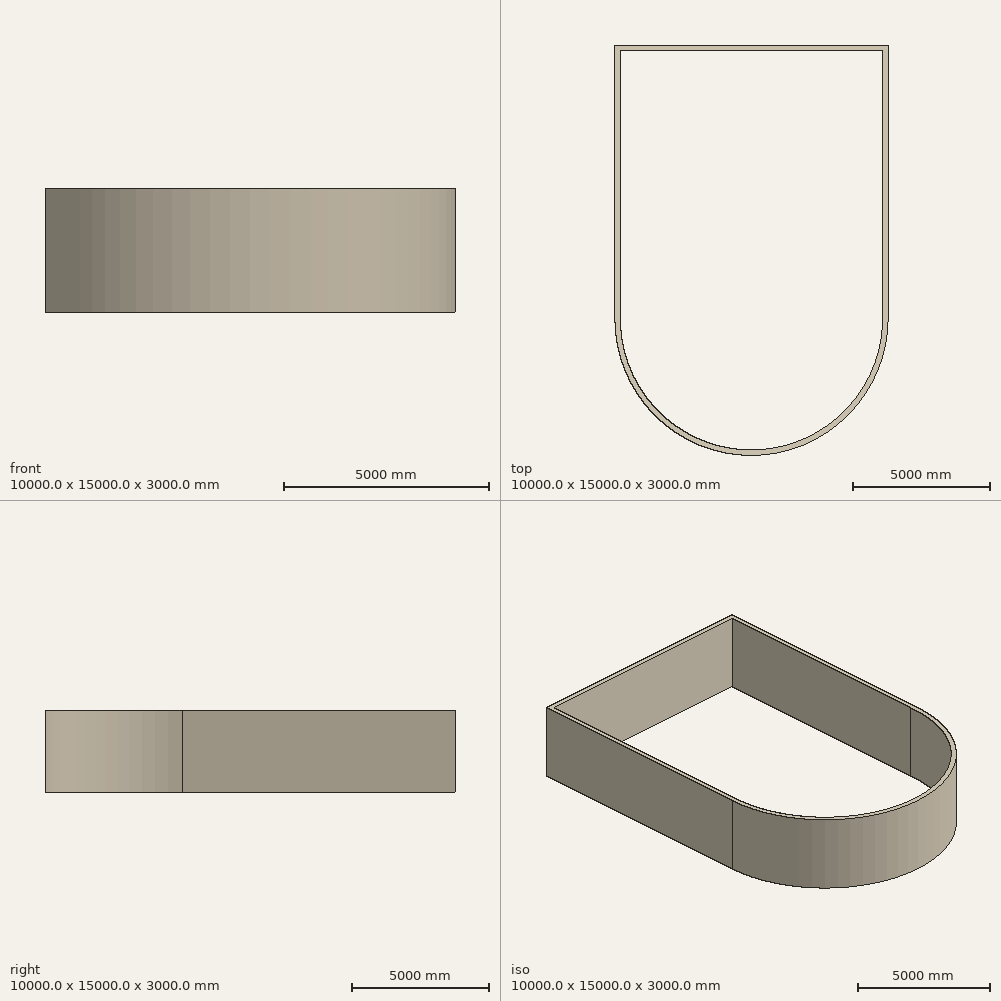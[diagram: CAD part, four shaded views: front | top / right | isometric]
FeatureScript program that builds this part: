
annotation { "Feature Type Name" : "Feature", "Feature Type Description" : "" }
export const myFeature = defineFeature(function(context is Context, id is Id, definition is map)
    precondition{}
    {
        {
            var Q0;
            Q0=qCreatedBy(makeId("Top.planeOp"),FACE);
            var sketch = newSketch(context, id + "F0", { "sketchPlane" : qUnion([Q0])});
            skLineSegment(sketch, "E0.bottom", {"start": v(-5000, 5000) * mm, "end": v(5000, 5000) * mm});
            skLineSegment(sketch, "E0.top", {"start": v(-5000, -5000) * mm, "end": v(5000, -5000) * mm});
            skLineSegment(sketch, "E0.left", {"start": v(-5000, 5000) * mm, "end": v(-5000, -5000) * mm});
            skLineSegment(sketch, "E0.right", {"start": v(5000, 5000) * mm, "end": v(5000, -5000) * mm});
            skPoint(sketch, "E0.middle", {"position": v(0, 0) * mm});
            skCircle(sketch, "E1", {"center": v(0, -5000) * mm, "radius": 5000 * mm});
            skCircle(sketch, "E2", {"center": v(0, -5000) * mm, "radius": 4800 * mm});
            skLineSegment(sketch, "E3.bottom", {"start": v(-4800, 4800) * mm, "end": v(4800, 4800) * mm});
            skLineSegment(sketch, "E3.top", {"start": v(-4800, -4800) * mm, "end": v(4800, -4800) * mm});
            skLineSegment(sketch, "E3.left", {"start": v(-4800, 4800) * mm, "end": v(-4800, -4800) * mm});
            skLineSegment(sketch, "E3.right", {"start": v(4800, 4800) * mm, "end": v(4800, -4800) * mm});
            skSolve(sketch);
        }
        {
            var Q0;
            Q0=makeQuery(id+"F0.imprint","IMPRINT",FACE,{"disambiguationData":[TD([[makeQuery(id+"F0.imprint","IMPRINT",EDGE,{"derivedFrom":sQuery(id+"F0.wireOp",EDGE,"E0.bottom")}),-1.0]])]});
            var Q1;
            {var subQ3=sQuery(id+"F0.wireOp",EDGE,"E2");var subQ5=sQuery(id+"F0.wireOp",EDGE,"E0.top");var subQ6=makeQuery(id+"F0.imprint","INTERSECT",VERTEX,{"disambiguationData":[OD(0.0)],"derivedFrom":[subQ5,subQ3]});Q1=makeQuery(id+"F0.imprint","IMPRINT",FACE,{"disambiguationData":[TD([[makeQuery(id+"F0.imprint","IMPRINT",EDGE,{"disambiguationData":[TD([[subQ6,1.0]])],"derivedFrom":subQ3}),-1.0]])]});}
            var Q2;
            {var subQ3=sQuery(id+"F0.wireOp",EDGE,"E2");var subQ6=sQuery(id+"F0.wireOp",EDGE,"E0.top");var subQ9=makeQuery(id+"F0.imprint","INTERSECT",VERTEX,{"disambiguationData":[OD(1.0)],"derivedFrom":[subQ6,subQ3]});Q2=makeQuery(id+"F0.imprint","IMPRINT",FACE,{"disambiguationData":[TD([[makeQuery(id+"F0.imprint","IMPRINT",EDGE,{"disambiguationData":[TD([[subQ9,-1.0]])],"derivedFrom":subQ3}),-1.0]])]});}
            var Q3;
            {var subQ1=sQuery(id+"F0.wireOp",EDGE,"E0.top");var subQ3=sQuery(id+"F0.wireOp",EDGE,"E2");var subQ4=makeQuery(id+"F0.imprint","INTERSECT",VERTEX,{"disambiguationData":[OD(0.0)],"derivedFrom":[subQ1,subQ3]});Q3=makeQuery(id+"F0.imprint","IMPRINT",FACE,{"disambiguationData":[TD([[makeQuery(id+"F0.imprint","IMPRINT",EDGE,{"disambiguationData":[TD([[subQ4,-1.0]])],"derivedFrom":subQ3}),-1.0]])]});}
            extrude(context, id + "F1", {"entities" : qUnion([Q0, Q1, Q2, Q3]), "depth" : 3000 * mm, "offsetDistance" : 25 * mm});
        }
    });
